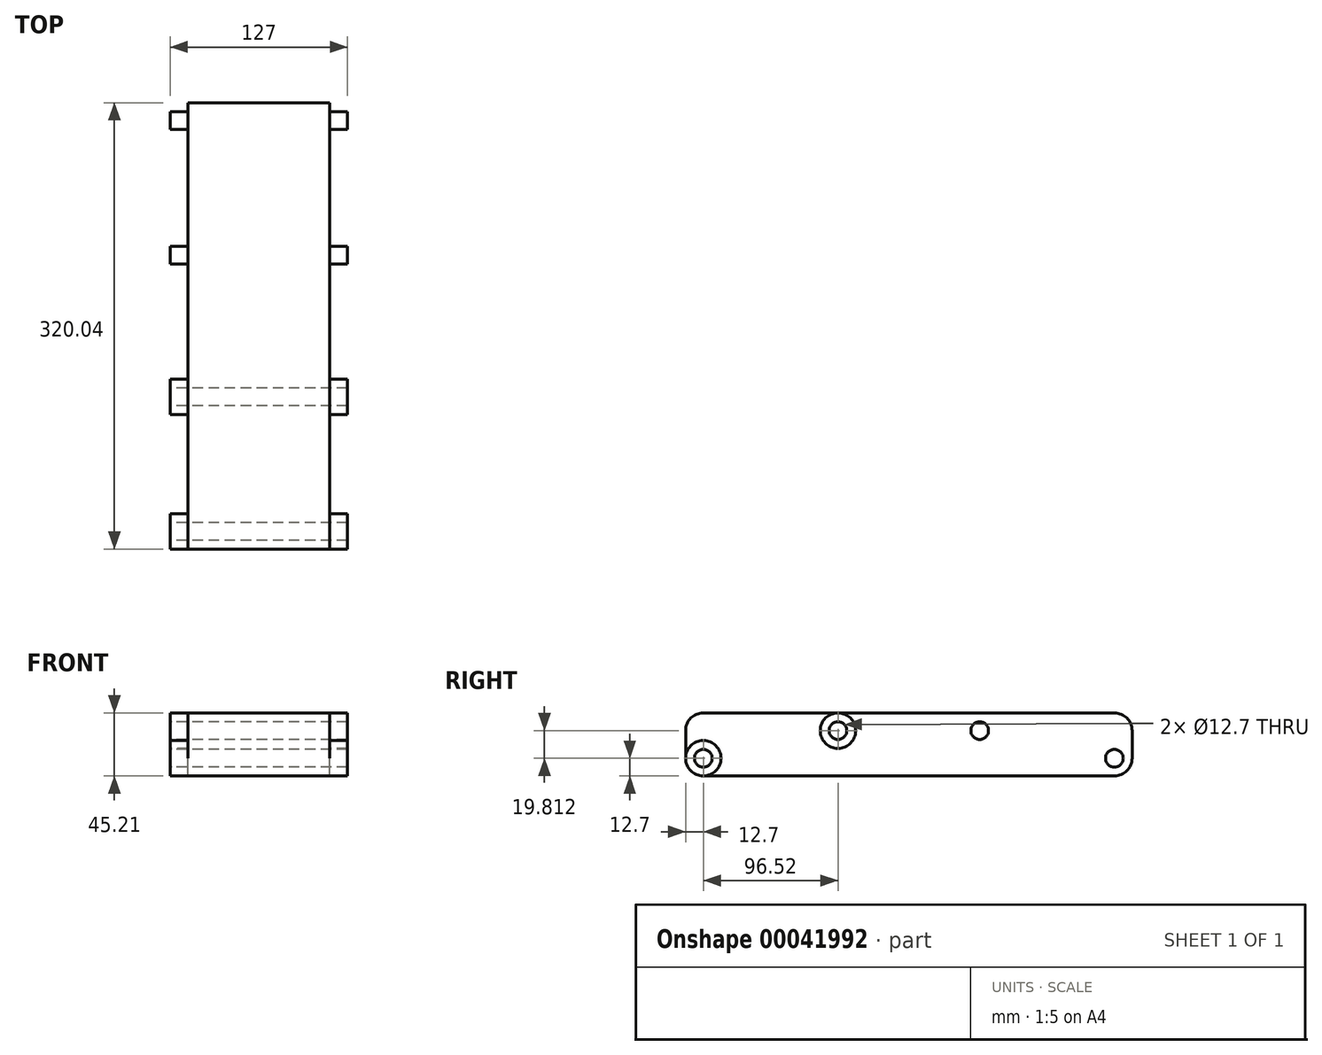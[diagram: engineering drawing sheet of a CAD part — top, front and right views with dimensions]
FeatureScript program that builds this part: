
annotation { "Feature Type Name" : "Feature", "Feature Type Description" : "" }
export const myFeature = defineFeature(function(context is Context, id is Id, definition is map)
    precondition{}
    {
        {
            var Q0;
            Q0=qCreatedBy(makeId("Right.planeOp"),FACE);
            var sketch = newSketch(context, id + "F0", { "sketchPlane" : qUnion([Q0])});
            skCircle(sketch, "E0", {"center": v(0, 0) * mm, "radius": 6.35 * mm});
            skLineSegment(sketch, "E1", {"start": v(0, 0) * mm, "end": v(96.52, 0) * mm, "construction": true});
            skLineSegment(sketch, "E2", {"start": v(96.52, 0) * mm, "end": v(96.52, 19.81) * mm, "construction": true});
            skCircle(sketch, "E3", {"center": v(96.52, 19.81) * mm, "radius": 6.35 * mm});
            skLineSegment(sketch, "E4.top", {"start": v(0, 19.81) * mm, "end": v(96.52, 19.81) * mm, "construction": true});
            skLineSegment(sketch, "E4.left", {"start": v(0, 0) * mm, "end": v(0, 19.81) * mm, "construction": true});
            skLineSegment(sketch, "E5.0", {"start": v(0, 32.51) * mm, "end": v(147.32, 32.51) * mm});
            skLineSegment(sketch, "E5.1", {"start": v(-12.7, 0) * mm, "end": v(-12.7, 19.81) * mm});
            skLineSegment(sketch, "E5.2", {"start": v(0, -12.7) * mm, "end": v(147.32, -12.7) * mm});
            skPoint(sketch, "E6.visualSharp", {"position": v(-12.7, 32.51) * mm});
            skArc(sketch, "E6.filletArc", {"start": v(0, 32.51) * mm, "mid": v(-8.98, 28.8) * mm, "end": v(-12.7, 19.81) * mm});
            skPoint(sketch, "E7.visualSharp", {"position": v(-12.7, -12.7) * mm});
            skArc(sketch, "E7.filletArc", {"start": v(-12.7, 0) * mm, "mid": v(-8.98, -8.98) * mm, "end": v(0, -12.7) * mm});
            skLineSegment(sketch, "E8", {"start": v(147.32, 33.62) * mm, "end": v(147.32, -20.88) * mm, "construction": true});
            skLineSegment(sketch, "E9.MirrorCS", {"start": v(294.64, 0) * mm, "end": v(294.64, 19.81) * mm, "construction": true});
            skArc(sketch, "E10.MirrorCS", {"start": v(307.34, 0) * mm, "mid": v(303.62, -8.98) * mm, "end": v(294.64, -12.7) * mm});
            skPoint(sketch, "E11.MirrorP", {"position": v(307.34, -12.7) * mm});
            skArc(sketch, "E12.MirrorCS", {"start": v(294.64, 32.51) * mm, "mid": v(303.62, 28.8) * mm, "end": v(307.34, 19.81) * mm});
            skLineSegment(sketch, "E13.MirrorCS", {"start": v(294.64, -12.7) * mm, "end": v(147.32, -12.7) * mm});
            skLineSegment(sketch, "E14.MirrorCS", {"start": v(307.34, 0) * mm, "end": v(307.34, 19.81) * mm});
            skLineSegment(sketch, "E15.MirrorCS", {"start": v(294.64, 32.51) * mm, "end": v(147.32, 32.51) * mm});
            skLineSegment(sketch, "E16.MirrorCS", {"start": v(294.64, 19.81) * mm, "end": v(198.12, 19.81) * mm, "construction": true});
            skCircle(sketch, "E17.MirrorC", {"center": v(198.12, 19.81) * mm, "radius": 6.35 * mm});
            skLineSegment(sketch, "E18.MirrorCS", {"start": v(198.12, 0) * mm, "end": v(198.12, 19.81) * mm, "construction": true});
            skLineSegment(sketch, "E19.MirrorCS", {"start": v(294.64, 0) * mm, "end": v(198.12, 0) * mm, "construction": true});
            skCircle(sketch, "E20.MirrorC", {"center": v(294.64, 0) * mm, "radius": 6.35 * mm});
            skPoint(sketch, "E21.MirrorP", {"position": v(307.34, 32.51) * mm});
            skSolve(sketch);
        }
        {
            var Q0;
            Q0=makeQuery(id+"F0.imprint","IMPRINT",FACE,{"disambiguationData":[TD([[makeQuery(id+"F0.imprint","IMPRINT",EDGE,{"derivedFrom":sQuery(id+"F0.wireOp",EDGE,"E0")}),-1.0]])]});
            extrude(context, id + "F1", {"entities" : qUnion([Q0]), "depth" : 101.6 * mm});
        }
        {
            var Q0;
            Q0=makeQuery(id+"F1.opExtrude","CAP_FACE",FACE,{"disambiguationData":[OSD([sQuery(id+"F0.wireOp",EDGE,"E0"),sQuery(id+"F0.wireOp",EDGE,"E3"),sQuery(id+"F0.wireOp",EDGE,"E5.0"),sQuery(id+"F0.wireOp",EDGE,"E5.1"),sQuery(id+"F0.wireOp",EDGE,"E5.2"),sQuery(id+"F0.wireOp",EDGE,"E5.3"),sQuery(id+"F0.wireOp",EDGE,"E6.filletArc"),sQuery(id+"F0.wireOp",EDGE,"E7.filletArc"),sQuery(id+"F0.wireOp",EDGE,"b346007b-a222-4b96-930d-faff9232e1b8.filletArc"),sQuery(id+"F0.wireOp",EDGE,"f4f6d976-239a-4716-a38e-df65e61f1000.filletArc")])],"isStart":false});
            var sketch = newSketch(context, id + "F2", { "sketchPlane" : qUnion([Q0])});
            skCircle(sketch, "E22", {"center": v(0, 0) * mm, "radius": 12.7 * mm});
            skCircle(sketch, "E23", {"center": v(0, 0) * mm, "radius": 6.35 * mm});
            skCircle(sketch, "E24", {"center": v(96.52, 19.81) * mm, "radius": 12.7 * mm});
            skCircle(sketch, "E25", {"center": v(96.52, 19.81) * mm, "radius": 6.35 * mm});
            skLineSegment(sketch, "E26", {"start": v(147.32, 32.51) * mm, "end": v(147.32, 4.02) * mm, "construction": true});
            skCircle(sketch, "E27.MirrorC", {"center": v(294.64, 0) * mm, "radius": 6.35 * mm});
            skCircle(sketch, "E28.MirrorC", {"center": v(294.64, 0) * mm, "radius": 12.7 * mm});
            skCircle(sketch, "E29.MirrorC", {"center": v(198.12, 19.81) * mm, "radius": 6.35 * mm});
            skCircle(sketch, "E30.MirrorC", {"center": v(198.12, 19.81) * mm, "radius": 12.7 * mm});
            skSolve(sketch);
        }
        {
            var Q0;
            Q0=makeQuery(id+"F2.imprint","IMPRINT",FACE,{"disambiguationData":[TD([[makeQuery(id+"F2.imprint","IMPRINT",EDGE,{"derivedFrom":sQuery(id+"F2.wireOp",EDGE,"E23")}),-1.0]])]});
            var Q1;
            Q1=makeQuery(id+"F2.imprint","IMPRINT",FACE,{"disambiguationData":[TD([[makeQuery(id+"F2.imprint","IMPRINT",EDGE,{"derivedFrom":sQuery(id+"F2.wireOp",EDGE,"E25")}),-1.0]])]});
            var Q2;
            Q2=makeQuery(id+"F2.imprint","IMPRINT",FACE,{"disambiguationData":[TD([[makeQuery(id+"F2.imprint","IMPRINT",EDGE,{"derivedFrom":sQuery(id+"F2.wireOp",EDGE,"E29.MirrorC")}),1.0]])]});
            var Q3;
            Q3=makeQuery(id+"F2.imprint","IMPRINT",FACE,{"disambiguationData":[TD([[makeQuery(id+"F2.imprint","IMPRINT",EDGE,{"derivedFrom":sQuery(id+"F2.wireOp",EDGE,"E27.MirrorC")}),1.0]])]});
            extrude(context, id + "F3", {"entities" : qUnion([Q0, Q1, Q2, Q3]), "operationType" : NewBodyOperationType.ADD, "depth" : 12.7 * mm, "hasSecondDirection" : true, "secondDirectionOppositeDirection" : true, "secondDirectionDepth" : 114.3 * mm});
        }
    });
